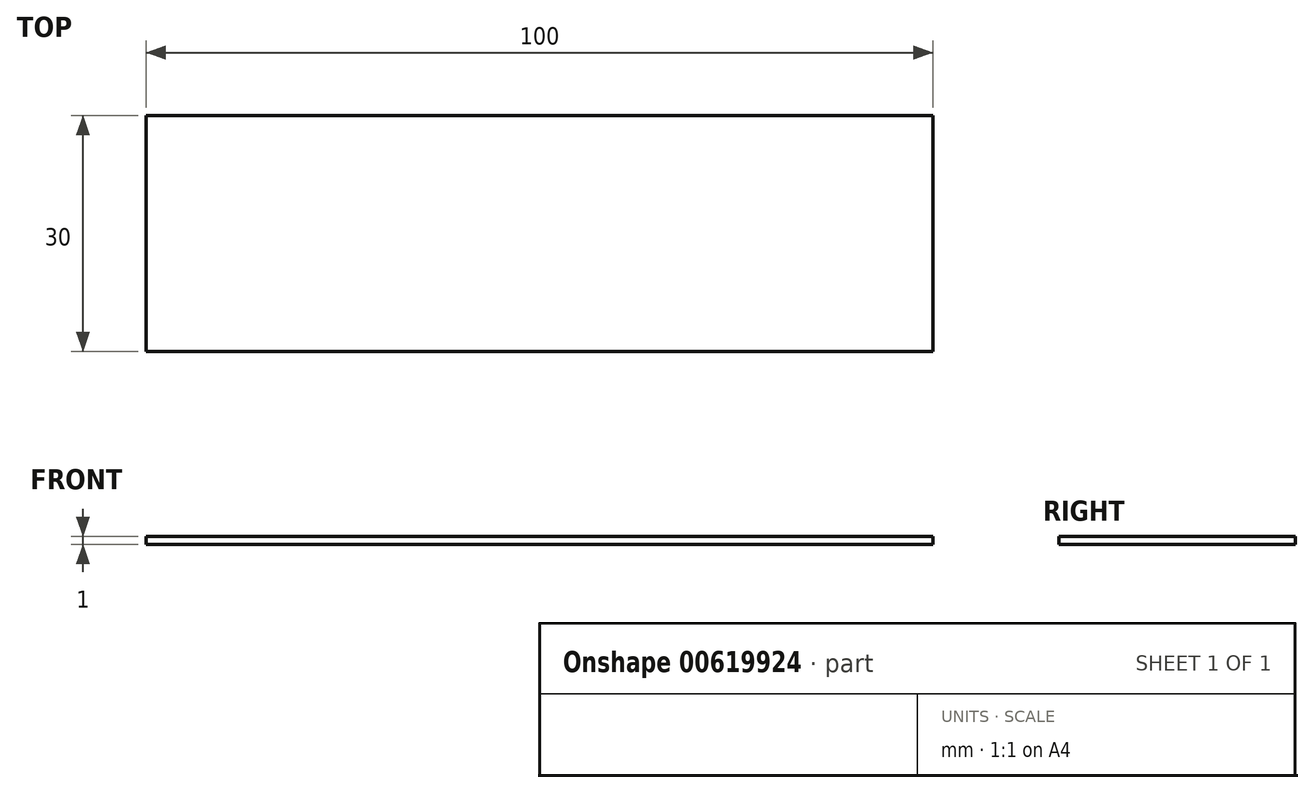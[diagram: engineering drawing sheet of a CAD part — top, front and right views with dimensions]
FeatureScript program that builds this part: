
annotation { "Feature Type Name" : "Feature", "Feature Type Description" : "" }
export const myFeature = defineFeature(function(context is Context, id is Id, definition is map)
    precondition{}
    {
        {
            var Q0;
            Q0=qCreatedBy(makeId("Top.planeOp"),FACE);
            var sketch = newSketch(context, id + "F0", { "sketchPlane" : qUnion([Q0])});
            skLineSegment(sketch, "E0.bottom", {"start": v(0, 0) * mm, "end": v(100, 0) * mm});
            skLineSegment(sketch, "E0.top", {"start": v(0, 30) * mm, "end": v(100, 30) * mm});
            skLineSegment(sketch, "E0.left", {"start": v(0, 0) * mm, "end": v(0, 30) * mm});
            skLineSegment(sketch, "E0.right", {"start": v(100, 0) * mm, "end": v(100, 30) * mm});
            skSolve(sketch);
        }
        {
            var Q0;
            Q0 = qSketchRegion(id + "F0", true);
            extrude(context, id + "F1", {"entities" : qUnion([Q0]), "depth" : 1 * mm, "offsetDistance" : 25.4 * mm});
        }
    });
